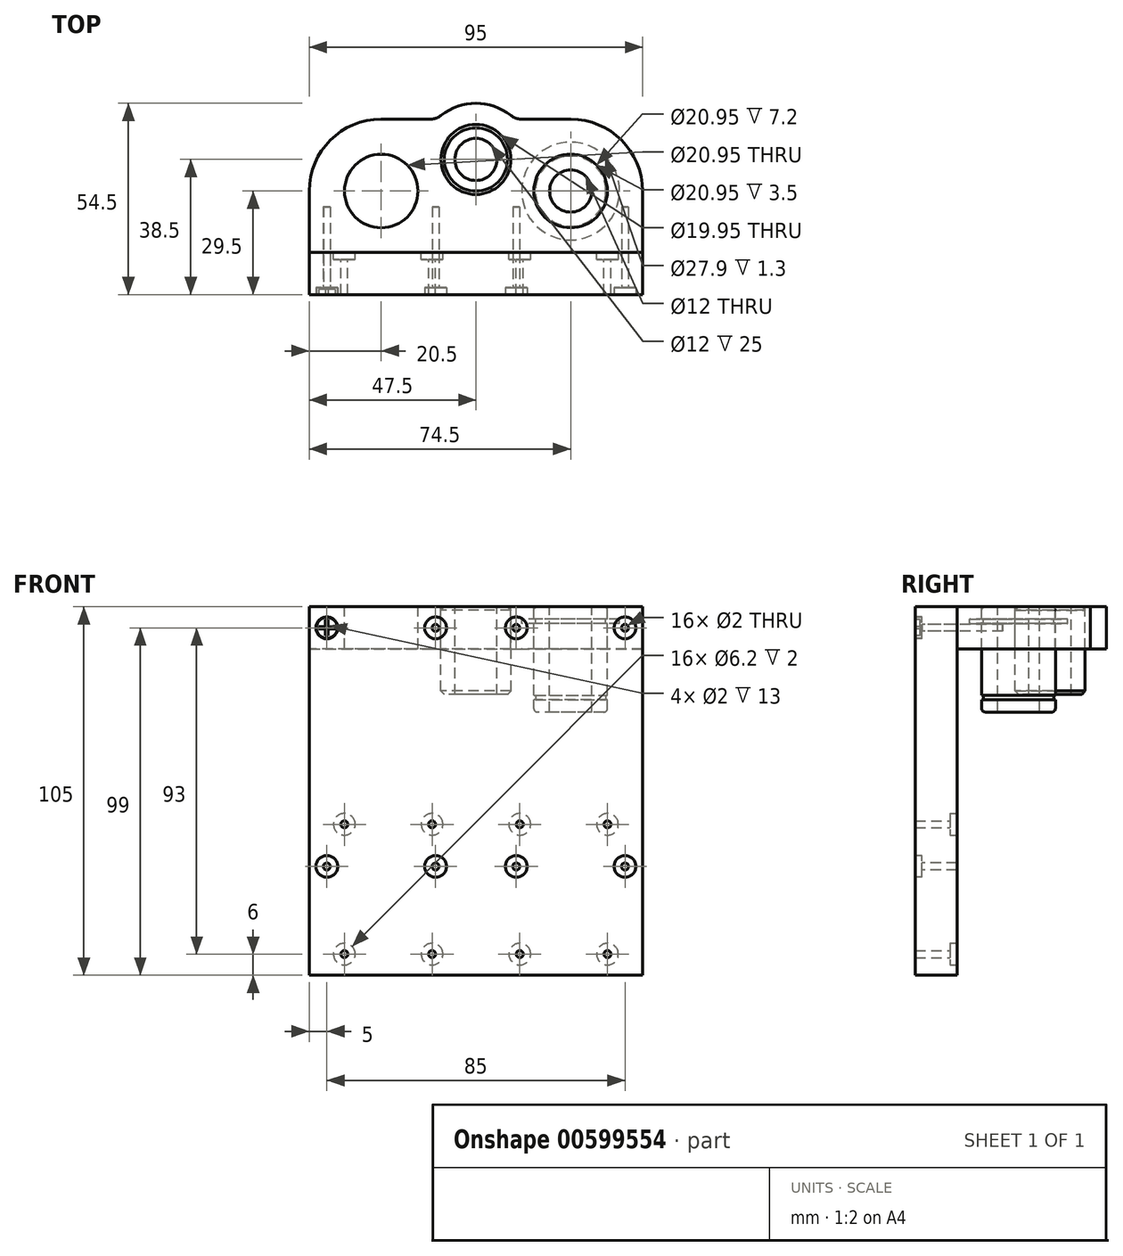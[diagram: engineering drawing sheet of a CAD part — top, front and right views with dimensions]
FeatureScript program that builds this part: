
annotation { "Feature Type Name" : "Feature", "Feature Type Description" : "" }
export const myFeature = defineFeature(function(context is Context, id is Id, definition is map)
    precondition{}
    {
        {
            var Q0;
            Q0=qCreatedBy(makeId("Front.planeOp"),FACE);
            var sketch = newSketch(context, id + "F0", { "sketchPlane" : qUnion([Q0])});
            skLineSegment(sketch, "E0.bottom", {"start": v(-47.5, 0) * mm, "end": v(47.5, 0) * mm});
            skLineSegment(sketch, "E0.top", {"start": v(-47.5, 80) * mm, "end": v(47.5, 80) * mm});
            skLineSegment(sketch, "E0.left", {"start": v(-47.5, 0) * mm, "end": v(-47.5, 80) * mm});
            skLineSegment(sketch, "E0.right", {"start": v(47.5, 0) * mm, "end": v(47.5, 80) * mm});
            skSolve(sketch);
        }
        {
            var Q0;
            Q0 = qSketchRegion(id + "F0", true);
            extrude(context, id + "F1", {"entities" : qUnion([Q0]), "oppositeDirection" : true, "depth" : 12 * mm, "offsetDistance" : 25 * mm});
        }
        {
            var Q0;
            Q0=makeQuery(id+"F1.opExtrude","SWEPT_FACE",FACE,{"disambiguationData":[OSD([sQuery(id+"F0.wireOp",EDGE,"E0.top")])]});
            var sketch = newSketch(context, id + "F2", { "sketchPlane" : qUnion([Q0])});
            skLineSegment(sketch, "E1.bottom", {"start": v(47.5, 12) * mm, "end": v(-47.5, 12) * mm});
            skLineSegment(sketch, "E1.top", {"start": v(27, 50) * mm, "end": v(-27, 50) * mm});
            skLineSegment(sketch, "E1.left", {"start": v(47.5, 12) * mm, "end": v(47.5, 29.5) * mm});
            skLineSegment(sketch, "E1.right", {"start": v(-47.5, 12) * mm, "end": v(-47.5, 29.5) * mm});
            skLineSegment(sketch, "E2", {"start": v(0, 12) * mm, "end": v(0, 50) * mm, "construction": true});
            skPoint(sketch, "E3.centerSnap0", {"position": v(0, 31) * mm});
            skArc(sketch, "E4.filletArc", {"start": v(47.5, 29.5) * mm, "mid": v(41.5, 44) * mm, "end": v(27, 50) * mm});
            skPoint(sketch, "E5.visualSharp", {"position": v(-47.5, 50) * mm});
            skArc(sketch, "E5.filletArc", {"start": v(-27, 50) * mm, "mid": v(-41.5, 44) * mm, "end": v(-47.5, 29.5) * mm});
            skCircle(sketch, "E6", {"center": v(27, 29.5) * mm, "radius": 10.47 * mm});
            skCircle(sketch, "E7.MirrorC", {"center": v(-27, 29.5) * mm, "radius": 10.47 * mm});
            skCircle(sketch, "E8", {"center": v(0, 38.5) * mm, "radius": 16 * mm});
            skSolve(sketch);
        }
        {
            var Q0;
            Q0 = qSketchRegion(id + "F2", true);
            extrude(context, id + "F3", {"entities" : qUnion([Q0]), "oppositeDirection" : true, "depth" : 12 * mm, "offsetDistance" : 25 * mm});
        }
        {
            var Q0;
            Q0=makeQuery(id+"F3.opExtrude","CAP_FACE",FACE,{"disambiguationData":[OSD([sQuery(id+"F2.wireOp",EDGE,"E1.bottom"),sQuery(id+"F2.wireOp",EDGE,"E1.top"),sQuery(id+"F2.wireOp",EDGE,"E1.left"),sQuery(id+"F2.wireOp",EDGE,"E1.right"),sQuery(id+"F2.wireOp",EDGE,"E4.filletArc"),sQuery(id+"F2.wireOp",EDGE,"E5.filletArc"),sQuery(id+"F2.wireOp",EDGE,"E6"),sQuery(id+"F2.wireOp",EDGE,"E7.MirrorC")])],"isStart":true});
            var sketch = newSketch(context, id + "F4", { "sketchPlane" : qUnion([Q0])});
            skCircle(sketch, "E9", {"center": v(0, 38.5) * mm, "radius": 9.97 * mm});
            skSolve(sketch);
        }
        {
            var Q0;
            Q0 = qSketchRegion(id + "F4", true);
            extrude(context, id + "F5", {"entities" : qUnion([Q0]), "operationType" : NewBodyOperationType.REMOVE, "oppositeDirection" : true, "depth" : 25 * mm, "offsetDistance" : 25 * mm});
        }
        {
            var Q0;
            Q0=makeQuery(id+"F3.opExtrude","CAP_FACE",FACE,{"disambiguationData":[OSD([sQuery(id+"F2.wireOp",EDGE,"E1.bottom"),sQuery(id+"F2.wireOp",EDGE,"E1.top"),sQuery(id+"F2.wireOp",EDGE,"E1.left"),sQuery(id+"F2.wireOp",EDGE,"E1.right"),sQuery(id+"F2.wireOp",EDGE,"E3"),sQuery(id+"F2.wireOp",EDGE,"E4.filletArc"),sQuery(id+"F2.wireOp",EDGE,"E5.filletArc"),sQuery(id+"F2.wireOp",EDGE,"cdc9c876-c57f-4e5e-8f0d-edd7876a0e1e0.MirrorC")])],"isStart":true});
            var sketch = newSketch(context, id + "F6", { "sketchPlane" : qUnion([Q0])});
            skCircle(sketch, "E10", {"center": v(27, 29.5) * mm, "radius": 10.5 * mm});
            skCircle(sketch, "E11", {"center": v(27, 29.5) * mm, "radius": 6 * mm});
            skSolve(sketch);
        }
        {
            var Q0;
            Q0 = qSketchRegion(id + "F6", true);
            extrude(context, id + "F7", {"entities" : qUnion([Q0]), "oppositeDirection" : true, "depth" : 30 * mm, "offsetDistance" : 25 * mm});
        }
        {
            var Q0;
            Q0=makeQuery(id+"F7.opExtrude","CAP_FACE",FACE,{"disambiguationData":[OSD([sQuery(id+"F6.wireOp",EDGE,"E10"),sQuery(id+"F6.wireOp",EDGE,"E11")])],"isStart":true});
            var sketch = newSketch(context, id + "F8", { "sketchPlane" : qUnion([Q0])});
            skCircle(sketch, "E12", {"center": v(27, 29.5) * mm, "radius": 10 * mm});
            skCircle(sketch, "E13", {"center": v(27, 29.5) * mm, "radius": 13.95 * mm});
            skSolve(sketch);
        }
        {
            var Q0;
            Q0 = qSketchRegion(id + "F8", true);
            extrude(context, id + "F9", {"entities" : qUnion([Q0]), "operationType" : NewBodyOperationType.REMOVE, "oppositeDirection" : true, "depth" : 4.8 * mm, "offsetDistance" : 25 * mm, "hasSecondDirection" : true, "secondDirectionOppositeDirection" : true, "secondDirectionDepth" : 3.5 * mm});
        }
        {
            var Q0;
            Q0=makeQuery(id+"F7.opExtrude","CAP_FACE",FACE,{"disambiguationData":[OSD([sQuery(id+"F6.wireOp",EDGE,"E10"),sQuery(id+"F6.wireOp",EDGE,"E11")])],"isStart":false});
            var sketch = newSketch(context, id + "F10", { "sketchPlane" : qUnion([Q0])});
            skCircle(sketch, "E14", {"center": v(27, -29.5) * mm, "radius": 10 * mm});
            skCircle(sketch, "E15", {"center": v(27, -29.5) * mm, "radius": 14.7 * mm});
            skSolve(sketch);
        }
        {
            var Q0;
            Q0 = qSketchRegion(id + "F10", true);
            extrude(context, id + "F11", {"entities" : qUnion([Q0]), "operationType" : NewBodyOperationType.REMOVE, "oppositeDirection" : true, "depth" : 4.8 * mm, "offsetDistance" : 25 * mm, "hasSecondDirection" : true, "secondDirectionOppositeDirection" : true, "secondDirectionDepth" : 3.5 * mm});
        }
        {
            var Q0;
            Q0=makeQuery(id+"F7.opExtrude","CAP_EDGE",EDGE,{"disambiguationData":[OSD([sQuery(id+"F6.wireOp",EDGE,"E10")])],"isStart":true});
            var Q1;
            Q1=makeQuery(id+"F7.opExtrude","CAP_EDGE",EDGE,{"disambiguationData":[OSD([sQuery(id+"F6.wireOp",EDGE,"E10")])],"isStart":false});
            fillet(context, id + "F12", {"entities" : qUnion([Q0, Q1]), "radius" : 1 * mm, "tangentPropagation" : true, "allowEdgeOverflow" : false});
        }
        {
            var Q0;
            Q0=makeQuery(id+"F1.opExtrude","CAP_FACE",FACE,{"disambiguationData":[OSD([sQuery(id+"F0.wireOp",EDGE,"E0.bottom"),sQuery(id+"F0.wireOp",EDGE,"E0.top"),sQuery(id+"F0.wireOp",EDGE,"E0.left"),sQuery(id+"F0.wireOp",EDGE,"E0.right")])],"isStart":true});
            var sketch = newSketch(context, id + "F13", { "sketchPlane" : qUnion([Q0])});
            skCircle(sketch, "E16", {"center": v(-42.5, 74) * mm, "radius": 1 * mm});
            skLineSegment(sketch, "E17", {"start": v(0, 80) * mm, "end": v(0, 68) * mm, "construction": true});
            skPoint(sketch, "E17.endSnap0", {"position": v(0, 80) * mm});
            skCircle(sketch, "E18.1.0.0", {"center": v(-11.5, 74) * mm, "radius": 1 * mm});
            skLineSegment(sketch, "E18.direction1", {"start": v(-42.5, 74) * mm, "end": v(-11.5, 74) * mm, "construction": true});
            skCircle(sketch, "E19.MirrorC", {"center": v(11.5, 74) * mm, "radius": 1 * mm});
            skCircle(sketch, "E20.MirrorC", {"center": v(42.5, 74) * mm, "radius": 1 * mm});
            skLineSegment(sketch, "E21", {"start": v(-47.5, 40) * mm, "end": v(47.5, 40) * mm, "construction": true});
            skCircle(sketch, "E22.MirrorC", {"center": v(-42.5, 6) * mm, "radius": 1 * mm});
            skCircle(sketch, "E23.MirrorC", {"center": v(-11.5, 6) * mm, "radius": 1 * mm});
            skCircle(sketch, "E24.MirrorC", {"center": v(11.5, 6) * mm, "radius": 1 * mm});
            skCircle(sketch, "E25.MirrorC", {"center": v(42.5, 6) * mm, "radius": 1 * mm});
            skSolve(sketch);
        }
        {
            var Q0;
            Q0 = qSketchRegion(id + "F13", true);
            extrude(context, id + "F14", {"entities" : qUnion([Q0]), "operationType" : NewBodyOperationType.REMOVE, "oppositeDirection" : true, "depth" : 25 * mm, "offsetDistance" : 25 * mm});
        }
        {
            var Q0;
            Q0=makeQuery(id+"F1.opExtrude","CAP_FACE",FACE,{"disambiguationData":[OSD([sQuery(id+"F0.wireOp",EDGE,"E0.bottom"),sQuery(id+"F0.wireOp",EDGE,"E0.top"),sQuery(id+"F0.wireOp",EDGE,"E0.left"),sQuery(id+"F0.wireOp",EDGE,"E0.right")])],"isStart":true});
            var sketch = newSketch(context, id + "F15", { "sketchPlane" : qUnion([Q0])});
            skCircle(sketch, "E26", {"center": v(-42.5, 74) * mm, "radius": 3.1 * mm});
            skCircle(sketch, "E27.1.0.0", {"center": v(-11.5, 74) * mm, "radius": 3.1 * mm});
            skLineSegment(sketch, "E28", {"start": v(0, 80) * mm, "end": v(0, 0) * mm, "construction": true});
            skLineSegment(sketch, "E29", {"start": v(47.5, 40) * mm, "end": v(-47.5, 40) * mm, "construction": true});
            skCircle(sketch, "E30.MirrorC", {"center": v(11.5, 74) * mm, "radius": 3.1 * mm});
            skCircle(sketch, "E31.MirrorC", {"center": v(42.5, 74) * mm, "radius": 3.1 * mm});
            skCircle(sketch, "E32.MirrorC", {"center": v(-42.5, 6) * mm, "radius": 3.1 * mm});
            skCircle(sketch, "E33.MirrorC", {"center": v(-11.5, 6) * mm, "radius": 3.1 * mm});
            skCircle(sketch, "E34.MirrorC", {"center": v(11.5, 6) * mm, "radius": 3.1 * mm});
            skCircle(sketch, "E35.MirrorC", {"center": v(42.5, 6) * mm, "radius": 3.1 * mm});
            skSolve(sketch);
        }
        {
            var Q0;
            Q0 = qSketchRegion(id + "F15", true);
            extrude(context, id + "F16", {"entities" : qUnion([Q0]), "operationType" : NewBodyOperationType.REMOVE, "oppositeDirection" : true, "depth" : 2 * mm, "offsetDistance" : 25 * mm});
        }
        {
            var Q0;
            Q0=makeQuery(id+"F1.opExtrude","CAP_FACE",FACE,{"disambiguationData":[OSD([sQuery(id+"F0.wireOp",EDGE,"E0.bottom"),sQuery(id+"F0.wireOp",EDGE,"E0.top"),sQuery(id+"F0.wireOp",EDGE,"E0.left"),sQuery(id+"F0.wireOp",EDGE,"E0.right")])],"isStart":true});
            var sketch = newSketch(context, id + "F17", { "sketchPlane" : qUnion([Q0])});
            skCircle(sketch, "E36", {"center": v(-42.5, 74) * mm, "radius": 3 * mm});
            skSolve(sketch);
        }
        {
            var Q0;
            Q0 = qSketchRegion(id + "F17", true);
            extrude(context, id + "F18", {"entities" : qUnion([Q0]), "oppositeDirection" : true, "depth" : 2 * mm, "offsetDistance" : 25 * mm});
        }
        {
            var Q0;
            Q0=makeQuery(id+"F18.opExtrude","CAP_FACE",FACE,{"disambiguationData":[OSD([sQuery(id+"F17.wireOp",EDGE,"E36")])],"isStart":false});
            var sketch = newSketch(context, id + "F19", { "sketchPlane" : qUnion([Q0])});
            skCircle(sketch, "E37", {"center": v(42.5, 74) * mm, "radius": 0.95 * mm});
            skSolve(sketch);
        }
        {
            var Q0;
            Q0 = qSketchRegion(id + "F19", true);
            extrude(context, id + "F20", {"entities" : qUnion([Q0]), "operationType" : NewBodyOperationType.ADD, "depth" : 23 * mm, "offsetDistance" : 25 * mm});
        }
        {
            var Q0;
            Q0=makeQuery(id+"F18.opExtrude","CAP_FACE",FACE,{"disambiguationData":[OSD([sQuery(id+"F17.wireOp",EDGE,"E36")])],"isStart":true});
            var sketch = newSketch(context, id + "F21", { "sketchPlane" : qUnion([Q0])});
            skLineSegment(sketch, "E38.bottom", {"start": v(-40.15, 74.35) * mm, "end": v(-42.15, 74.35) * mm});
            skLineSegment(sketch, "E38.top", {"start": v(-40.15, 73.65) * mm, "end": v(-42.15, 73.65) * mm});
            skLineSegment(sketch, "E38.left", {"start": v(-40.15, 74.35) * mm, "end": v(-40.15, 73.65) * mm});
            skLineSegment(sketch, "E38.right", {"start": v(-44.85, 74.35) * mm, "end": v(-44.85, 73.65) * mm});
            skLineSegment(sketch, "E39.bottom", {"start": v(-42.15, 71.78) * mm, "end": v(-42.85, 71.78) * mm});
            skLineSegment(sketch, "E39.top", {"start": v(-42.15, 76.35) * mm, "end": v(-42.85, 76.35) * mm});
            skLineSegment(sketch, "E39.left", {"start": v(-42.15, 71.78) * mm, "end": v(-42.15, 73.65) * mm});
            skLineSegment(sketch, "E39.right", {"start": v(-42.85, 71.78) * mm, "end": v(-42.85, 73.65) * mm});
            skLineSegment(sketch, "E40", {"start": v(-42.5, 74) * mm, "end": v(-42.5, 76.35) * mm, "construction": true});
            skLineSegment(sketch, "E41", {"start": v(-40.15, 74) * mm, "end": v(-42.5, 74) * mm, "construction": true});
            skLineSegment(sketch, "E42.trimOffspring", {"start": v(-42.85, 73.65) * mm, "end": v(-44.85, 73.65) * mm});
            skLineSegment(sketch, "E43.trimOffspring", {"start": v(-42.85, 74.35) * mm, "end": v(-42.85, 76.35) * mm});
            skLineSegment(sketch, "E44.trimOffspring", {"start": v(-42.85, 74.35) * mm, "end": v(-44.85, 74.35) * mm});
            skLineSegment(sketch, "E45.trimOffspring", {"start": v(-42.15, 74.35) * mm, "end": v(-42.15, 76.35) * mm});
            skSolve(sketch);
        }
        {
            var Q0;
            Q0 = qSketchRegion(id + "F21", true);
            extrude(context, id + "F22", {"entities" : qUnion([Q0]), "operationType" : NewBodyOperationType.REMOVE, "oppositeDirection" : true, "depth" : 1.5 * mm, "offsetDistance" : 25 * mm});
        }
        {
            var Q0;
            Q0=makeQuery(id+"F1.opExtrude","CAP_FACE",FACE,{"disambiguationData":[OSD([sQuery(id+"F0.wireOp",EDGE,"E0.bottom"),sQuery(id+"F0.wireOp",EDGE,"E0.top"),sQuery(id+"F0.wireOp",EDGE,"E0.left"),sQuery(id+"F0.wireOp",EDGE,"E0.right")])],"isStart":true});
            var sketch = newSketch(context, id + "F23", { "sketchPlane" : qUnion([Q0])});
            skLineSegment(sketch, "E46.bottom", {"start": v(-47.5, 0) * mm, "end": v(47.5, 0) * mm});
            skLineSegment(sketch, "E46.top", {"start": v(-47.5, -25) * mm, "end": v(47.5, -25) * mm});
            skLineSegment(sketch, "E46.left", {"start": v(-47.5, 0) * mm, "end": v(-47.5, -25) * mm});
            skLineSegment(sketch, "E46.right", {"start": v(47.5, 0) * mm, "end": v(47.5, -25) * mm});
            skSolve(sketch);
        }
        {
            var Q0;
            Q0 = qSketchRegion(id + "F23", true);
            extrude(context, id + "F24", {"entities" : qUnion([Q0]), "operationType" : NewBodyOperationType.ADD, "oppositeDirection" : true, "depth" : 12 * mm, "offsetDistance" : 25 * mm});
        }
        {
            var Q0;
            Q0=makeQuery(id+"F1.opExtrude","CAP_FACE",FACE,{"disambiguationData":[OSD([sQuery(id+"F0.wireOp",EDGE,"E0.bottom"),sQuery(id+"F0.wireOp",EDGE,"E0.top"),sQuery(id+"F0.wireOp",EDGE,"E0.left"),sQuery(id+"F0.wireOp",EDGE,"E0.right")])],"isStart":false});
            var sketch = newSketch(context, id + "F25", { "sketchPlane" : qUnion([Q0])});
            skCircle(sketch, "E47", {"center": v(-37.5, -19) * mm, "radius": 1 * mm});
            skCircle(sketch, "E48.0.1.0", {"center": v(-37.5, 18) * mm, "radius": 1 * mm});
            skCircle(sketch, "E48.1.0.0", {"center": v(-12.5, -19) * mm, "radius": 1 * mm});
            skCircle(sketch, "E48.1.1.0", {"center": v(-12.5, 18) * mm, "radius": 1 * mm});
            skCircle(sketch, "E48.2.0.0", {"center": v(12.5, -19) * mm, "radius": 1 * mm});
            skCircle(sketch, "E48.2.1.0", {"center": v(12.5, 18) * mm, "radius": 1 * mm});
            skCircle(sketch, "E48.3.0.0", {"center": v(37.5, -19) * mm, "radius": 1 * mm});
            skCircle(sketch, "E48.3.1.0", {"center": v(37.5, 18) * mm, "radius": 1 * mm});
            skLineSegment(sketch, "E48.direction1", {"start": v(-37.5, -19) * mm, "end": v(-12.5, -19) * mm, "construction": true});
            skLineSegment(sketch, "E48.direction2", {"start": v(-37.5, -19) * mm, "end": v(-37.5, 18) * mm, "construction": true});
            skCircle(sketch, "E49", {"center": v(-42.5, 6) * mm, "radius": 1.66 * mm, "construction": true});
            skSolve(sketch);
        }
        {
            var Q0;
            Q0 = qSketchRegion(id + "F25", true);
            extrude(context, id + "F26", {"entities" : qUnion([Q0]), "operationType" : NewBodyOperationType.REMOVE, "oppositeDirection" : true, "depth" : 25 * mm, "offsetDistance" : 25 * mm});
        }
        {
            var Q0;
            Q0=makeQuery(id+"F1.opExtrude","CAP_FACE",FACE,{"disambiguationData":[OSD([sQuery(id+"F0.wireOp",EDGE,"E0.bottom"),sQuery(id+"F0.wireOp",EDGE,"E0.top"),sQuery(id+"F0.wireOp",EDGE,"E0.left"),sQuery(id+"F0.wireOp",EDGE,"E0.right")])],"isStart":false});
            var sketch = newSketch(context, id + "F27", { "sketchPlane" : qUnion([Q0])});
            skCircle(sketch, "E50", {"center": v(-37.5, 18) * mm, "radius": 3.1 * mm});
            skCircle(sketch, "E51.0.1.0", {"center": v(-37.5, -19) * mm, "radius": 3.1 * mm});
            skCircle(sketch, "E51.1.0.0", {"center": v(-12.5, 18) * mm, "radius": 3.1 * mm});
            skCircle(sketch, "E51.1.1.0", {"center": v(-12.5, -19) * mm, "radius": 3.1 * mm});
            skCircle(sketch, "E51.2.0.0", {"center": v(12.5, 18) * mm, "radius": 3.1 * mm});
            skCircle(sketch, "E51.2.1.0", {"center": v(12.5, -19) * mm, "radius": 3.1 * mm});
            skCircle(sketch, "E51.3.0.0", {"center": v(37.5, 18) * mm, "radius": 3.1 * mm});
            skCircle(sketch, "E51.3.1.0", {"center": v(37.5, -19) * mm, "radius": 3.1 * mm});
            skLineSegment(sketch, "E51.direction1", {"start": v(-37.5, 18) * mm, "end": v(-12.5, 18) * mm, "construction": true});
            skLineSegment(sketch, "E51.direction2", {"start": v(-37.5, 18) * mm, "end": v(-37.5, -19) * mm, "construction": true});
            skSolve(sketch);
        }
        {
            var Q0;
            Q0 = qSketchRegion(id + "F27", true);
            extrude(context, id + "F28", {"entities" : qUnion([Q0]), "operationType" : NewBodyOperationType.REMOVE, "oppositeDirection" : true, "depth" : 2 * mm, "offsetDistance" : 25 * mm});
        }
        {
            var Q0;
            Q0=makeQuery(id+"F3.opExtrude","CAP_FACE",FACE,{"disambiguationData":[OSD([sQuery(id+"F2.wireOp",EDGE,"E1.bottom"),sQuery(id+"F2.wireOp",EDGE,"E1.top"),sQuery(id+"F2.wireOp",EDGE,"E1.left"),sQuery(id+"F2.wireOp",EDGE,"E1.right"),sQuery(id+"F2.wireOp",EDGE,"E4.filletArc"),sQuery(id+"F2.wireOp",EDGE,"E5.filletArc"),sQuery(id+"F2.wireOp",EDGE,"E6"),sQuery(id+"F2.wireOp",EDGE,"E7.MirrorC")])],"isStart":true});
            var sketch = newSketch(context, id + "F29", { "sketchPlane" : qUnion([Q0])});
            skCircle(sketch, "E52", {"center": v(0, 38.5) * mm, "radius": 10 * mm});
            skCircle(sketch, "E53", {"center": v(0, 38.5) * mm, "radius": 6 * mm});
            skSolve(sketch);
        }
        {
            var Q0;
            Q0 = qSketchRegion(id + "F29", true);
            extrude(context, id + "F30", {"entities" : qUnion([Q0]), "oppositeDirection" : true, "depth" : 25 * mm, "offsetDistance" : 25 * mm});
        }
        {
            var Q0;
            Q0=makeQuery(id+"F30.opExtrude","CAP_EDGE",EDGE,{"disambiguationData":[OSD([sQuery(id+"F29.wireOp",EDGE,"E52")])],"isStart":false});
            var Q1;
            Q1=makeQuery(id+"F30.opExtrude","CAP_EDGE",EDGE,{"disambiguationData":[OSD([sQuery(id+"F29.wireOp",EDGE,"E52")])],"isStart":true});
            chamfer(context, id + "F31", {"entities" : qUnion([Q0, Q1]), "width" : 1 * mm, "tangentPropagation" : true});
        }
        {
            var Q0;
            {var subQ0=sQuery(id+"F2.wireOp",EDGE,"E8");var subQ1=sQuery(id+"F2.wireOp",EDGE,"E1.top");Q0=makeQuery(id+"F3.opExtrude","SWEPT_EDGE",EDGE,{"disambiguationData":[OSD([subQ1,subQ0]),TDD([makeQuery(id+"F2.imprint","INTERSECT",VERTEX,{"disambiguationData":[OD(0.0)],"derivedFrom":[subQ1,subQ0]})])]});}
            var Q1;
            {var subQ0=sQuery(id+"F2.wireOp",EDGE,"E8");var subQ1=sQuery(id+"F2.wireOp",EDGE,"E1.top");Q1=makeQuery(id+"F3.opExtrude","SWEPT_EDGE",EDGE,{"disambiguationData":[OSD([subQ1,subQ0]),TDD([makeQuery(id+"F2.imprint","INTERSECT",VERTEX,{"disambiguationData":[OD(1.0)],"derivedFrom":[subQ1,subQ0]})])]});}
            fillet(context, id + "F32", {"entities" : qUnion([Q0, Q1]), "radius" : 5 * mm, "tangentPropagation" : true, "allowEdgeOverflow" : false});
        }
    });
